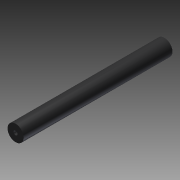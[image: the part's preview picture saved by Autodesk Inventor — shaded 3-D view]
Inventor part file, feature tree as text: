
AUTODESK INVENTOR PART (.ipt)
format: ipt  version: 2012 (Build 160160000, 160)  size: 70,144 bytes
history: native  units: in
note: dims shown in document units (in); Inventor stores cm internally (conversion verified against a paired STEP export)
features: extrude x1, sketch x1
ambient origin geometry x8: Origin, YZ Plane, XZ Plane, XY Plane, X Axis, Y Axis, Z Axis, Center Point
bodies: Solid1 (feature_tree)
feature tree (2):
  extrude  "Extrusion1"  Depth=2.0in
  sketch  "Sketch1"  dims[d0=0.5in d1=2.0in d2=18.5in d3=0.0in]
